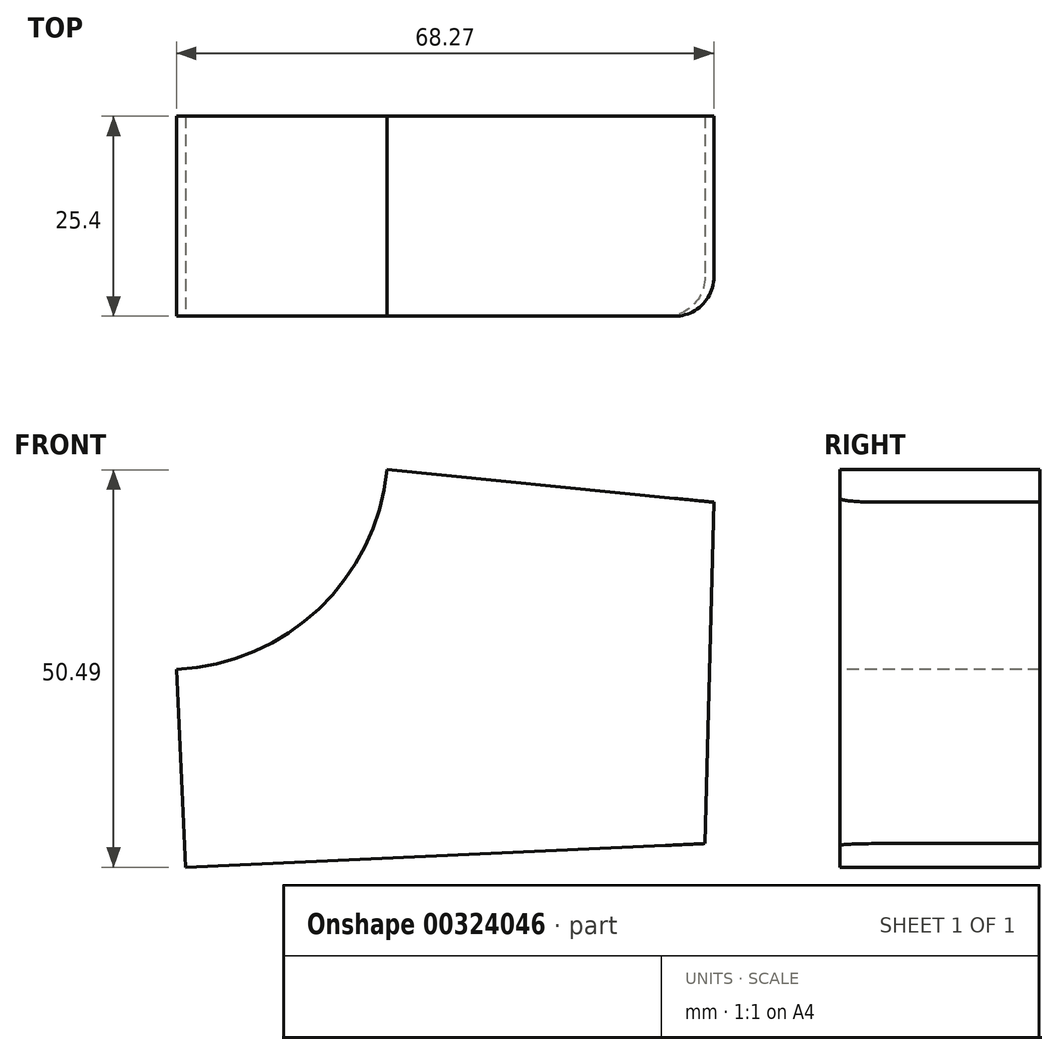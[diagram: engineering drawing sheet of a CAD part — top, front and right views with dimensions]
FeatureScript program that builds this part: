
annotation { "Feature Type Name" : "Feature", "Feature Type Description" : "" }
export const myFeature = defineFeature(function(context is Context, id is Id, definition is map)
    precondition{}
    {
        {
            var Q0;
            Q0=qCreatedBy(makeId("Front.planeOp"),FACE);
            var sketch = newSketch(context, id + "F0", { "sketchPlane" : qUnion([Q0])});
            skCircle(sketch, "E0", {"center": v(-68.42, 39.14) * mm, "radius": 28.17 * mm});
            skLineSegment(sketch, "E1", {"start": v(-68.42, 39.14) * mm, "end": v(-66, -14.14) * mm});
            skLineSegment(sketch, "E2", {"start": v(-66, -14.14) * mm, "end": v(0, -11.14) * mm});
            skLineSegment(sketch, "E3", {"start": v(0, -11.14) * mm, "end": v(1.12, 32.23) * mm});
            skLineSegment(sketch, "E4", {"start": v(1.12, 32.23) * mm, "end": v(-68.42, 39.14) * mm});
            skSolve(sketch);
        }
        {
            var Q0;
            {var subQ0=sQuery(id+"F0.wireOp",EDGE,"E2");Q0=makeQuery(id+"F0.imprint","IMPRINT",FACE,{"disambiguationData":[TD([[makeQuery(id+"F0.imprint","IMPRINT",EDGE,{"derivedFrom":subQ0}),1.0]])]});}
            extrude(context, id + "F1", {"entities" : qUnion([Q0]), "oppositeDirection" : true, "depth" : 25.4 * mm});
        }
        {
            var Q0;
            Q0=makeQuery(id+"F1.opExtrude","CAP_EDGE",EDGE,{"disambiguationData":[OSD([sQuery(id+"F0.wireOp",EDGE,"E3")])],"isStart":true});
            fillet(context, id + "F2", {"entities" : qUnion([Q0]), "radius" : 5 * mm, "tangentPropagation" : true, "allowEdgeOverflow" : false});
        }
    });
